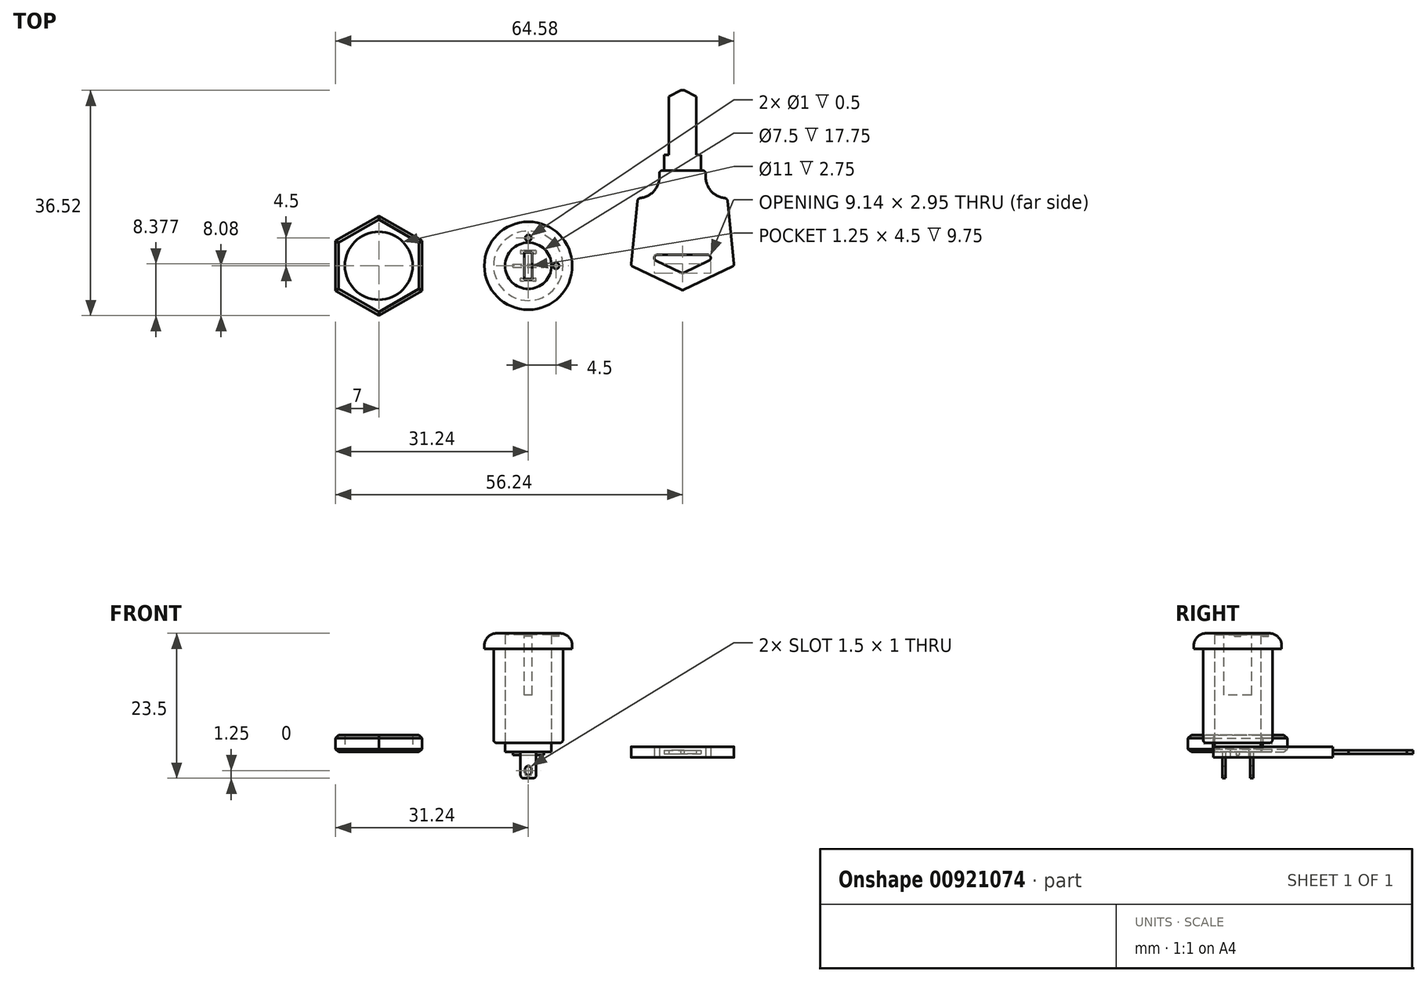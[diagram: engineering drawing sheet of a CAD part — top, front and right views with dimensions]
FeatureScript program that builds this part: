
annotation { "Feature Type Name" : "Feature", "Feature Type Description" : "" }
export const myFeature = defineFeature(function(context is Context, id is Id, definition is map)
    precondition{}
    {
        {
            var Q0;
            Q0=qCreatedBy(makeId("Top.planeOp"),FACE);
            var sketch = newSketch(context, id + "F0", { "sketchPlane" : qUnion([Q0])});
            skCircle(sketch, "E0", {"center": v(0, 0) * mm, "radius": 5.62 * mm});
            skCircle(sketch, "E1", {"center": v(0, 0) * mm, "radius": 7.12 * mm});
            skCircle(sketch, "E2", {"center": v(0, 0) * mm, "radius": 3.75 * mm});
            skSolve(sketch);
        }
        {
            var Q0;
            Q0=makeQuery(id+"F0.imprint","IMPRINT",FACE,{"disambiguationData":[TD([[makeQuery(id+"F0.imprint","IMPRINT",EDGE,{"derivedFrom":sQuery(id+"F0.wireOp",EDGE,"E2")}),1.0]])]});
            extrude(context, id + "F1", {"entities" : qUnion([Q0]), "depth" : 1.5 * mm, "offsetDistance" : 25 * mm});
        }
        {
            var Q0;
            Q0=makeQuery(id+"F0.imprint","IMPRINT",FACE,{"disambiguationData":[TD([[makeQuery(id+"F0.imprint","IMPRINT",EDGE,{"derivedFrom":sQuery(id+"F0.wireOp",EDGE,"E0")}),1.0]])]});
            var Q1;
            Q1=makeQuery(id+"F1.opExtrude","CAP_FACE",FACE,{"disambiguationData":[OSD([sQuery(id+"F0.wireOp",EDGE,"E2")])],"isStart":false});
            extrude(context, id + "F2", {"entities" : qUnion([Q0]), "depth" : 16.75 * mm, "offsetDistance" : 25 * mm, "hasSecondDirection" : true, "secondDirectionBound" : SecondDirectionBoundingType.UP_TO_SURFACE, "secondDirectionOppositeDirection" : false, "secondDirectionDepth" : 1.5 * mm, "secondDirectionBoundEntityFace" : qUnion([Q1])});
        }
        {
            var Q0;
            Q0=makeQuery(id+"F0.imprint","IMPRINT",FACE,{"disambiguationData":[TD([[makeQuery(id+"F0.imprint","IMPRINT",EDGE,{"derivedFrom":sQuery(id+"F0.wireOp",EDGE,"E0")}),-1.0]])]});
            var Q1;
            Q1=makeQuery(id+"F0.imprint","IMPRINT",FACE,{"disambiguationData":[TD([[makeQuery(id+"F0.imprint","IMPRINT",EDGE,{"derivedFrom":sQuery(id+"F0.wireOp",EDGE,"E0")}),1.0]])]});
            var Q2;
            Q2=makeQuery(id+"F2.opExtrude","CAP_FACE",FACE,{"disambiguationData":[OSD([sQuery(id+"F0.wireOp",EDGE,"E0"),sQuery(id+"F0.wireOp",EDGE,"E2")])],"isStart":false});
            var Q3;
            Q3=makeQuery(id+"F2.opExtrude","CAP_FACE",FACE,{"disambiguationData":[OSD([sQuery(id+"F0.wireOp",EDGE,"E0"),sQuery(id+"F0.wireOp",EDGE,"E2")])],"isStart":false});
            extrude(context, id + "F3", {"entities" : qUnion([Q0, Q1]), "operationType" : NewBodyOperationType.ADD, "endBound" : BoundingType.UP_TO_SURFACE, "depth" : (16.75 + 2.5) * mm, "endBoundEntityFace" : qUnion([Q2]), "hasOffset" : true, "offsetDistance" : 2.5 * mm, "offsetOppositeDirection" : true, "hasSecondDirection" : true, "secondDirectionBound" : SecondDirectionBoundingType.UP_TO_SURFACE, "secondDirectionOppositeDirection" : false, "secondDirectionDepth" : 16.75 * mm, "secondDirectionBoundEntityFace" : qUnion([Q3])});
        }
        {
            var Q0;
            Q0=makeQuery(id+"F1.opExtrude","CAP_FACE",FACE,{"disambiguationData":[OSD([sQuery(id+"F0.wireOp",EDGE,"E2")])],"isStart":false});
            var Q1;
            Q1=makeQuery(id+"F3.opExtrude","CAP_FACE",FACE,{"disambiguationData":[OSD([sQuery(id+"F0.wireOp",EDGE,"E1"),sQuery(id+"F0.wireOp",EDGE,"E2")])],"isStart":false});
            extrude(context, id + "F4", {"entities" : qUnion([Q0]), "endBound" : BoundingType.UP_TO_SURFACE, "depth" : 25 * mm, "endBoundEntityFace" : qUnion([Q1]), "hasOffset" : true, "offsetDistance" : .25 * mm});
        }
        {
            var Q0;
            Q0=makeQuery(id+"F3.opExtrude","CAP_FACE",FACE,{"disambiguationData":[OSD([sQuery(id+"F0.wireOp",EDGE,"E1")])],"isStart":false});
            var sketch = newSketch(context, id + "F5", { "sketchPlane" : qUnion([Q0])});
            skCircle(sketch, "E3", {"center": v(0, 4.5) * mm, "radius": 0.5 * mm});
            skCircle(sketch, "E4", {"center": v(4.5, 0) * mm, "radius": 0.5 * mm});
            skLineSegment(sketch, "E5", {"start": v(0, 4.5) * mm, "end": v(0, 0) * mm, "construction": true});
            skLineSegment(sketch, "E6", {"start": v(0, 0) * mm, "end": v(4.5, 0) * mm, "construction": true});
            skCircle(sketch, "E7.0", {"center": v(0, 0) * mm, "radius": 3.75 * mm});
            skLineSegment(sketch, "E8.bottom", {"start": v(0.63, 2.25) * mm, "end": v(-0.62, 2.25) * mm});
            skLineSegment(sketch, "E8.top", {"start": v(0.62, -2.25) * mm, "end": v(-0.63, -2.25) * mm});
            skLineSegment(sketch, "E8.left", {"start": v(0.63, 2.25) * mm, "end": v(0.62, -2.25) * mm});
            skLineSegment(sketch, "E8.right", {"start": v(-0.62, 2.25) * mm, "end": v(-0.63, -2.25) * mm});
            skSolve(sketch);
        }
        {
            var Q0;
            Q0=makeQuery(id+"F5.imprint","IMPRINT",FACE,{"disambiguationData":[TD([[makeQuery(id+"F5.imprint","IMPRINT",EDGE,{"derivedFrom":sQuery(id+"F5.wireOp",EDGE,"E8.bottom")}),1.0]])]});
            extrude(context, id + "F6", {"entities" : qUnion([Q0]), "operationType" : NewBodyOperationType.REMOVE, "oppositeDirection" : true, "depth" : 10 * mm, "offsetDistance" : 25 * mm});
        }
        {
            var Q0;
            Q0=makeQuery(id+"F5.imprint","IMPRINT",FACE,{"disambiguationData":[TD([[makeQuery(id+"F5.imprint","IMPRINT",EDGE,{"derivedFrom":sQuery(id+"F5.wireOp",EDGE,"E3")}),1.0]])]});
            var Q1;
            Q1=makeQuery(id+"F5.imprint","IMPRINT",FACE,{"disambiguationData":[TD([[makeQuery(id+"F5.imprint","IMPRINT",EDGE,{"derivedFrom":sQuery(id+"F5.wireOp",EDGE,"E4")}),1.0]])]});
            extrude(context, id + "F7", {"entities" : qUnion([Q0, Q1]), "operationType" : NewBodyOperationType.REMOVE, "oppositeDirection" : true, "depth" : .5 * mm, "offsetDistance" : 25 * mm});
        }
        {
            var Q0;
            Q0=makeQuery(id+"F5.imprint","IMPRINT",FACE,{"disambiguationData":[TD([[makeQuery(id+"F5.imprint","IMPRINT",EDGE,{"derivedFrom":sQuery(id+"F5.wireOp",EDGE,"E3")}),1.0]])]});
            var Q1;
            Q1=makeQuery(id+"F5.imprint","IMPRINT",FACE,{"disambiguationData":[TD([[makeQuery(id+"F5.imprint","IMPRINT",EDGE,{"derivedFrom":sQuery(id+"F5.wireOp",EDGE,"E4")}),1.0]])]});
            var Q2;
            Q2=makeQuery(id+"F7.boolean.opBoolean","COPY",FACE,{"derivedFrom":makeQuery(id+"F7.opExtrude","CAP_FACE",FACE,{"disambiguationData":[OSD([sQuery(id+"F5.wireOp",EDGE,"E3")])],"isStart":false})});
            var Q3;
            Q3=makeQuery(id+"F7.boolean.opBoolean","COPY",FACE,{"derivedFrom":makeQuery(id+"F7.opExtrude","CAP_FACE",FACE,{"disambiguationData":[OSD([sQuery(id+"F5.wireOp",EDGE,"E3")])],"isStart":false})});
            extrude(context, id + "F8", {"entities" : qUnion([Q0, Q1]), "endBound" : BoundingType.UP_TO_SURFACE, "oppositeDirection" : true, "depth" : 25 * mm, "endBoundEntityFace" : qUnion([Q2]), "offsetDistance" : .25 * mm, "hasSecondDirection" : true, "secondDirectionBound" : SecondDirectionBoundingType.UP_TO_SURFACE, "secondDirectionOppositeDirection" : true, "secondDirectionDepth" : 25 * mm, "secondDirectionBoundEntityFace" : qUnion([Q3]), "hasSecondDirectionOffset" : true, "secondDirectionOffsetDistance" : .25 * mm});
        }
        {
            var Q0;
            Q0=qCreatedBy(makeId("Front.planeOp"),FACE);
            var sketch = newSketch(context, id + "F9", { "sketchPlane" : qUnion([Q0])});
            skLineSegment(sketch, "E9.bottom", {"start": v(1.25, 0) * mm, "end": v(-1.25, 0) * mm});
            skLineSegment(sketch, "E9.top", {"start": v(1.25, -4.25) * mm, "end": v(-1.25, -4.25) * mm});
            skLineSegment(sketch, "E9.left", {"start": v(1.25, 0) * mm, "end": v(1.25, -4.25) * mm});
            skLineSegment(sketch, "E9.right", {"start": v(-1.25, 0) * mm, "end": v(-1.25, -4.25) * mm});
            skPoint(sketch, "E10", {"position": v(0, 0) * mm});
            skLineSegment(sketch, "E11.bottom", {"start": v(-0.5, -2.25) * mm, "end": v(0.5, -2.25) * mm});
            skLineSegment(sketch, "E11.top", {"start": v(-0.5, -3.75) * mm, "end": v(0.5, -3.75) * mm});
            skLineSegment(sketch, "E11.left", {"start": v(-0.5, -2.25) * mm, "end": v(-0.5, -3.75) * mm});
            skLineSegment(sketch, "E11.right", {"start": v(0.5, -2.25) * mm, "end": v(0.5, -3.75) * mm});
            skPoint(sketch, "E11.middle", {"position": v(0, -3) * mm});
            skLineSegment(sketch, "E12.bottom", {"start": v(-2.5, 0) * mm, "end": v(2.5, 0) * mm});
            skLineSegment(sketch, "E12.top", {"start": v(-2.5, -0.5) * mm, "end": v(2.5, -0.5) * mm});
            skLineSegment(sketch, "E12.left", {"start": v(-2.5, 0) * mm, "end": v(-2.5, -0.5) * mm});
            skLineSegment(sketch, "E12.right", {"start": v(2.5, 0) * mm, "end": v(2.5, -0.5) * mm});
            skSolve(sketch);
        }
        {
            var Q0;
            {var subQ5=sQuery(id+"F9.wireOp",EDGE,"E12.left");Q0=makeQuery(id+"F9.imprint","IMPRINT",FACE,{"disambiguationData":[TD([[makeQuery(id+"F9.imprint","IMPRINT",EDGE,{"derivedFrom":subQ5}),1.0]])]});}
            var Q1;
            {var subQ0=sQuery(id+"F9.wireOp",EDGE,"E12.bottom");var subQ1=sQuery(id+"F9.wireOp",EDGE,"E9.left");var subQ2=makeQuery(id+"F9.imprint","INTERSECT",VERTEX,{"derivedFrom":[subQ1,subQ0]});Q1=makeQuery(id+"F9.imprint","IMPRINT",FACE,{"disambiguationData":[TD([[makeQuery(id+"F9.imprint","IMPRINT",EDGE,{"disambiguationData":[TD([[subQ2,-1.0]])],"derivedFrom":subQ1}),-1.0]])]});}
            var Q2;
            {var subQ5=sQuery(id+"F9.wireOp",EDGE,"E12.right");Q2=makeQuery(id+"F9.imprint","IMPRINT",FACE,{"disambiguationData":[TD([[makeQuery(id+"F9.imprint","IMPRINT",EDGE,{"derivedFrom":subQ5}),-1.0]])]});}
            extrude(context, id + "F10", {"entities" : qUnion([Q0, Q1, Q2]), "operationType" : NewBodyOperationType.ADD, "endBound" : BoundingType.SYMMETRIC, "depth" : .5 * mm, "offsetDistance" : 25 * mm});
        }
        {
            var Q0;
            {var subQ1=sQuery(id+"F9.wireOp",EDGE,"E9.top");Q0=makeQuery(id+"F9.imprint","IMPRINT",FACE,{"disambiguationData":[TD([[makeQuery(id+"F9.imprint","IMPRINT",EDGE,{"derivedFrom":subQ1}),-1.0]])]});}
            var Q1;
            {var subQ0=sQuery(id+"F9.wireOp",EDGE,"E12.bottom");var subQ1=sQuery(id+"F9.wireOp",EDGE,"E9.left");var subQ2=makeQuery(id+"F9.imprint","INTERSECT",VERTEX,{"derivedFrom":[subQ1,subQ0]});Q1=makeQuery(id+"F9.imprint","IMPRINT",FACE,{"disambiguationData":[TD([[makeQuery(id+"F9.imprint","IMPRINT",EDGE,{"disambiguationData":[TD([[subQ2,-1.0]])],"derivedFrom":subQ1}),-1.0]])]});}
            extrude(context, id + "F11", {"entities" : qUnion([Q0, Q1]), "depth" : 2.5 * mm, "offsetDistance" : 25 * mm, "hasSecondDirection" : true, "secondDirectionOppositeDirection" : false, "secondDirectionDepth" : 2 * mm});
        }
        {
            var Q0;
            {var subQ1=sQuery(id+"F9.wireOp",EDGE,"E9.top");Q0=makeQuery(id+"F9.imprint","IMPRINT",FACE,{"disambiguationData":[TD([[makeQuery(id+"F9.imprint","IMPRINT",EDGE,{"derivedFrom":subQ1}),-1.0]])]});}
            var Q1;
            {var subQ0=sQuery(id+"F9.wireOp",EDGE,"E12.bottom");var subQ1=sQuery(id+"F9.wireOp",EDGE,"E9.left");var subQ2=makeQuery(id+"F9.imprint","INTERSECT",VERTEX,{"derivedFrom":[subQ1,subQ0]});Q1=makeQuery(id+"F9.imprint","IMPRINT",FACE,{"disambiguationData":[TD([[makeQuery(id+"F9.imprint","IMPRINT",EDGE,{"disambiguationData":[TD([[subQ2,-1.0]])],"derivedFrom":subQ1}),-1.0]])]});}
            extrude(context, id + "F12", {"entities" : qUnion([Q0, Q1]), "oppositeDirection" : true, "depth" : 2.5 * mm, "offsetDistance" : 25 * mm, "hasSecondDirection" : true, "secondDirectionOppositeDirection" : true, "secondDirectionDepth" : 2 * mm});
        }
        {
            var Q0;
            Q0=makeQuery(id+"F3.opExtrude","CAP_EDGE",EDGE,{"disambiguationData":[OSD([sQuery(id+"F0.wireOp",EDGE,"E1")])],"isStart":false});
            fillet(context, id + "F13", {"entities" : qUnion([Q0]), "radius" : 2 * mm, "tangentPropagation" : true, "allowEdgeOverflow" : false});
        }
        {
            var Q0;
            Q0=makeQuery(id+"F12.opExtrude","SWEPT_EDGE",EDGE,{"disambiguationData":[OSD([sQuery(id+"F9.wireOp",EDGE,"E9.top"),sQuery(id+"F9.wireOp",EDGE,"E9.left")])]});
            var Q1;
            Q1=makeQuery(id+"F12.opExtrude","SWEPT_EDGE",EDGE,{"disambiguationData":[OSD([sQuery(id+"F9.wireOp",EDGE,"E9.top"),sQuery(id+"F9.wireOp",EDGE,"E9.right")])]});
            var Q2;
            Q2=makeQuery(id+"F11.opExtrude","SWEPT_EDGE",EDGE,{"disambiguationData":[OSD([sQuery(id+"F9.wireOp",EDGE,"E9.top"),sQuery(id+"F9.wireOp",EDGE,"E9.left")])]});
            var Q3;
            Q3=makeQuery(id+"F11.opExtrude","SWEPT_EDGE",EDGE,{"disambiguationData":[OSD([sQuery(id+"F9.wireOp",EDGE,"E9.top"),sQuery(id+"F9.wireOp",EDGE,"E9.right")])]});
            var Q4;
            Q4=makeQuery(id+"F2.opExtrude","CAP_EDGE",EDGE,{"disambiguationData":[OSD([sQuery(id+"F0.wireOp",EDGE,"E0")])],"isStart":true});
            var Q5;
            Q5=makeQuery(id+"F12.opExtrude","SWEPT_EDGE",EDGE,{"disambiguationData":[OSD([sQuery(id+"F9.wireOp",EDGE,"E11.bottom"),sQuery(id+"F9.wireOp",EDGE,"E11.left")])]});
            var Q6;
            Q6=makeQuery(id+"F12.opExtrude","SWEPT_EDGE",EDGE,{"disambiguationData":[OSD([sQuery(id+"F9.wireOp",EDGE,"E11.bottom"),sQuery(id+"F9.wireOp",EDGE,"E11.right")])]});
            var Q7;
            Q7=makeQuery(id+"F12.opExtrude","SWEPT_EDGE",EDGE,{"disambiguationData":[OSD([sQuery(id+"F9.wireOp",EDGE,"E11.top"),sQuery(id+"F9.wireOp",EDGE,"E11.right")])]});
            var Q8;
            Q8=makeQuery(id+"F12.opExtrude","SWEPT_EDGE",EDGE,{"disambiguationData":[OSD([sQuery(id+"F9.wireOp",EDGE,"E11.top"),sQuery(id+"F9.wireOp",EDGE,"E11.left")])]});
            var Q9;
            Q9=makeQuery(id+"F11.opExtrude","SWEPT_EDGE",EDGE,{"disambiguationData":[OSD([sQuery(id+"F9.wireOp",EDGE,"E11.bottom"),sQuery(id+"F9.wireOp",EDGE,"E11.left")])]});
            var Q10;
            Q10=makeQuery(id+"F11.opExtrude","SWEPT_EDGE",EDGE,{"disambiguationData":[OSD([sQuery(id+"F9.wireOp",EDGE,"E11.bottom"),sQuery(id+"F9.wireOp",EDGE,"E11.right")])]});
            var Q11;
            Q11=makeQuery(id+"F11.opExtrude","SWEPT_EDGE",EDGE,{"disambiguationData":[OSD([sQuery(id+"F9.wireOp",EDGE,"E11.top"),sQuery(id+"F9.wireOp",EDGE,"E11.right")])]});
            var Q12;
            Q12=makeQuery(id+"F11.opExtrude","SWEPT_EDGE",EDGE,{"disambiguationData":[OSD([sQuery(id+"F9.wireOp",EDGE,"E11.top"),sQuery(id+"F9.wireOp",EDGE,"E11.left")])]});
            fillet(context, id + "F14", {"entities" : qUnion([Q0, Q1, Q2, Q3, Q4, Q5, Q6, Q7, Q8, Q9, Q10, Q11, Q12]), "radius" : .5 * mm, "tangentPropagation" : true, "allowEdgeOverflow" : false});
        }
        {
            var Q0;
            Q0=qCreatedBy(makeId("Top.planeOp"),FACE);
            var sketch = newSketch(context, id + "F15", { "sketchPlane" : qUnion([Q0])});
            skCircle(sketch, "E13", {"center": v(-24.24, 0) * mm, "radius": 5.5 * mm});
            skCircle(sketch, "E14.cCircle", {"center": v(-24.24, 0) * mm, "radius": 7 * mm, "construction": true});
            skLineSegment(sketch, "E14.0", {"start": v(-31.24, -4.04) * mm, "end": v(-31.24, 4.04) * mm});
            skLineSegment(sketch, "E14.1", {"start": v(-31.24, 4.04) * mm, "end": v(-24.24, 8.08) * mm});
            skLineSegment(sketch, "E14.2", {"start": v(-24.24, 8.08) * mm, "end": v(-17.24, 4.04) * mm});
            skLineSegment(sketch, "E14.3", {"start": v(-17.24, 4.04) * mm, "end": v(-17.24, -4.04) * mm});
            skLineSegment(sketch, "E14.4", {"start": v(-17.24, -4.04) * mm, "end": v(-24.24, -8.08) * mm});
            skLineSegment(sketch, "E14.5", {"start": v(-24.24, -8.08) * mm, "end": v(-31.24, -4.04) * mm});
            skPoint(sketch, "E14.0.midPoint", {"position": v(-31.24, 0) * mm});
            skSolve(sketch);
        }
        {
            var Q0;
            Q0=makeQuery(id+"F15.imprint","IMPRINT",FACE,{"disambiguationData":[TD([[makeQuery(id+"F15.imprint","IMPRINT",EDGE,{"derivedFrom":sQuery(id+"F15.wireOp",EDGE,"E13")}),-1.0]])]});
            extrude(context, id + "F16", {"entities" : qUnion([Q0]), "depth" : 2.75 * mm, "offsetDistance" : 25 * mm});
        }
        {
            var Q0;
            Q0=makeQuery(id+"F16.opExtrude","CAP_EDGE",EDGE,{"disambiguationData":[OSD([sQuery(id+"F15.wireOp",EDGE,"E14.4")])],"isStart":false});
            var Q1;
            Q1=makeQuery(id+"F16.opExtrude","CAP_EDGE",EDGE,{"disambiguationData":[OSD([sQuery(id+"F15.wireOp",EDGE,"E14.5")])],"isStart":false});
            var Q2;
            Q2=makeQuery(id+"F16.opExtrude","CAP_EDGE",EDGE,{"disambiguationData":[OSD([sQuery(id+"F15.wireOp",EDGE,"E14.0")])],"isStart":false});
            var Q3;
            Q3=makeQuery(id+"F16.opExtrude","CAP_EDGE",EDGE,{"disambiguationData":[OSD([sQuery(id+"F15.wireOp",EDGE,"E14.1")])],"isStart":false});
            var Q4;
            Q4=makeQuery(id+"F16.opExtrude","CAP_EDGE",EDGE,{"disambiguationData":[OSD([sQuery(id+"F15.wireOp",EDGE,"E14.2")])],"isStart":false});
            var Q5;
            Q5=makeQuery(id+"F16.opExtrude","CAP_EDGE",EDGE,{"disambiguationData":[OSD([sQuery(id+"F15.wireOp",EDGE,"E14.3")])],"isStart":false});
            var Q6;
            Q6=makeQuery(id+"F16.opExtrude","CAP_EDGE",EDGE,{"disambiguationData":[OSD([sQuery(id+"F15.wireOp",EDGE,"E14.2")])],"isStart":true});
            var Q7;
            Q7=makeQuery(id+"F16.opExtrude","CAP_EDGE",EDGE,{"disambiguationData":[OSD([sQuery(id+"F15.wireOp",EDGE,"E14.1")])],"isStart":true});
            var Q8;
            Q8=makeQuery(id+"F16.opExtrude","CAP_EDGE",EDGE,{"disambiguationData":[OSD([sQuery(id+"F15.wireOp",EDGE,"E14.0")])],"isStart":true});
            var Q9;
            Q9=makeQuery(id+"F16.opExtrude","CAP_EDGE",EDGE,{"disambiguationData":[OSD([sQuery(id+"F15.wireOp",EDGE,"E14.5")])],"isStart":true});
            var Q10;
            Q10=makeQuery(id+"F16.opExtrude","CAP_EDGE",EDGE,{"disambiguationData":[OSD([sQuery(id+"F15.wireOp",EDGE,"E14.4")])],"isStart":true});
            var Q11;
            Q11=makeQuery(id+"F16.opExtrude","CAP_EDGE",EDGE,{"disambiguationData":[OSD([sQuery(id+"F15.wireOp",EDGE,"E14.3")])],"isStart":true});
            chamfer(context, id + "F17", {"entities" : qUnion([Q0, Q1, Q2, Q3, Q4, Q5, Q6, Q7, Q8, Q9, Q10, Q11]), "width" : .5 * mm, "tangentPropagation" : true});
        }
        {
            var Q0;
            Q0=qCreatedBy(makeId("Top.planeOp"),FACE);
            var sketch = newSketch(context, id + "F18", { "sketchPlane" : qUnion([Q0])});
            skLineSegment(sketch, "E15", {"start": v(16.63, 0) * mm, "end": v(25, -4) * mm});
            skLineSegment(sketch, "E16", {"start": v(25, -4) * mm, "end": v(33.38, 0) * mm});
            skLineSegment(sketch, "E17", {"start": v(33.38, 0) * mm, "end": v(32.25, 10.94) * mm});
            skLineSegment(sketch, "E18", {"start": v(16.63, 0) * mm, "end": v(17.75, 10.94) * mm});
            skArc(sketch, "E19", {"start": v(17.75, 10.94) * mm, "mid": v(20.56, 12.35) * mm, "end": v(21.13, 15.44) * mm});
            skArc(sketch, "E20", {"start": v(28.88, 15.44) * mm, "mid": v(29.44, 12.35) * mm, "end": v(32.25, 10.94) * mm});
            skLineSegment(sketch, "E21", {"start": v(21.13, 15.44) * mm, "end": v(28.88, 15.44) * mm});
            skLineSegment(sketch, "E22.0", {"start": v(25, -1.23) * mm, "end": v(31.28, 1.77) * mm});
            skLineSegment(sketch, "E22.1", {"start": v(18.72, 1.77) * mm, "end": v(25, -1.23) * mm});
            skLineSegment(sketch, "E23", {"start": v(18.72, 1.77) * mm, "end": v(31.28, 1.77) * mm});
            skLineSegment(sketch, "E24.bottom", {"start": v(27.25, 15.44) * mm, "end": v(22.75, 15.44) * mm});
            skLineSegment(sketch, "E24.top", {"start": v(27.25, 28.44) * mm, "end": v(22.75, 28.44) * mm});
            skLineSegment(sketch, "E24.left", {"start": v(27.25, 15.44) * mm, "end": v(27.25, 28.44) * mm});
            skLineSegment(sketch, "E24.right", {"start": v(22.75, 15.44) * mm, "end": v(22.75, 28.44) * mm});
            skPoint(sketch, "E25", {"position": v(25, 15.44) * mm});
            skLineSegment(sketch, "E26.bottom", {"start": v(22, 15.44) * mm, "end": v(28, 15.44) * mm});
            skLineSegment(sketch, "E26.top", {"start": v(22, 17.94) * mm, "end": v(28, 17.94) * mm});
            skLineSegment(sketch, "E26.left", {"start": v(22, 15.44) * mm, "end": v(22, 17.94) * mm});
            skLineSegment(sketch, "E26.right", {"start": v(28, 15.44) * mm, "end": v(28, 17.94) * mm});
            skSolve(sketch);
        }
        {
            var Q0;
            Q0=makeQuery(id+"F18.imprint","IMPRINT",FACE,{"disambiguationData":[TD([[makeQuery(id+"F18.imprint","IMPRINT",EDGE,{"derivedFrom":sQuery(id+"F18.wireOp",EDGE,"E15")}),1.0]])]});
            extrude(context, id + "F19", {"entities" : qUnion([Q0]), "endBound" : BoundingType.SYMMETRIC, "depth" : (3.5 / 2) * mm, "offsetDistance" : 25 * mm});
        }
        {
            var Q0;
            {var subQ0=sQuery(id+"F18.wireOp",EDGE,"E26.bottom");var subQ1=sQuery(id+"F18.wireOp",EDGE,"E24.left");var subQ2=makeQuery(id+"F18.imprint","INTERSECT",VERTEX,{"derivedFrom":[subQ1,subQ0]});Q0=makeQuery(id+"F18.imprint","IMPRINT",FACE,{"disambiguationData":[TD([[makeQuery(id+"F18.imprint","IMPRINT",EDGE,{"disambiguationData":[TD([[subQ2,-1.0]])],"derivedFrom":subQ1}),1.0]])]});}
            var Q1;
            {var subQ5=sQuery(id+"F18.wireOp",EDGE,"E26.right");Q1=makeQuery(id+"F18.imprint","IMPRINT",FACE,{"disambiguationData":[TD([[makeQuery(id+"F18.imprint","IMPRINT",EDGE,{"derivedFrom":subQ5}),1.0]])]});}
            var Q2;
            {var subQ5=sQuery(id+"F18.wireOp",EDGE,"E26.left");Q2=makeQuery(id+"F18.imprint","IMPRINT",FACE,{"disambiguationData":[TD([[makeQuery(id+"F18.imprint","IMPRINT",EDGE,{"derivedFrom":subQ5}),-1.0]])]});}
            var Q3;
            {var subQ0=sQuery(id+"F18.wireOp",EDGE,"E24.top");Q3=makeQuery(id+"F18.imprint","IMPRINT",FACE,{"disambiguationData":[TD([[makeQuery(id+"F18.imprint","IMPRINT",EDGE,{"derivedFrom":subQ0}),1.0]])]});}
            extrude(context, id + "F20", {"entities" : qUnion([Q0, Q1, Q2, Q3]), "endBound" : BoundingType.SYMMETRIC, "depth" : (1.25 / 2) * mm, "offsetDistance" : 25 * mm});
        }
        {
            var Q0;
            Q0=makeQuery(id+"F19.opExtrude","SWEPT_EDGE",EDGE,{"disambiguationData":[OSD([sQuery(id+"F18.wireOp",EDGE,"E22.1"),sQuery(id+"F18.wireOp",EDGE,"E23")])]});
            var Q1;
            Q1=makeQuery(id+"F19.opExtrude","SWEPT_EDGE",EDGE,{"disambiguationData":[OSD([sQuery(id+"F18.wireOp",EDGE,"E22.0"),sQuery(id+"F18.wireOp",EDGE,"E22.1")])]});
            var Q2;
            Q2=makeQuery(id+"F19.opExtrude","SWEPT_EDGE",EDGE,{"disambiguationData":[OSD([sQuery(id+"F18.wireOp",EDGE,"E22.0"),sQuery(id+"F18.wireOp",EDGE,"E23")])]});
            var Q3;
            Q3=makeQuery(id+"F19.opExtrude","SWEPT_EDGE",EDGE,{"disambiguationData":[OSD([sQuery(id+"F18.wireOp",EDGE,"E16"),sQuery(id+"F18.wireOp",EDGE,"E17")])]});
            var Q4;
            Q4=makeQuery(id+"F19.opExtrude","SWEPT_EDGE",EDGE,{"disambiguationData":[OSD([sQuery(id+"F18.wireOp",EDGE,"E15"),sQuery(id+"F18.wireOp",EDGE,"E16")])]});
            var Q5;
            Q5=makeQuery(id+"F19.opExtrude","SWEPT_EDGE",EDGE,{"disambiguationData":[OSD([sQuery(id+"F18.wireOp",EDGE,"E15"),sQuery(id+"F18.wireOp",EDGE,"E18")])]});
            var Q6;
            Q6=makeQuery(id+"F19.opExtrude","SWEPT_EDGE",EDGE,{"disambiguationData":[OSD([sQuery(id+"F18.wireOp",EDGE,"E17"),sQuery(id+"F18.wireOp",EDGE,"E20")])]});
            var Q7;
            Q7=makeQuery(id+"F19.opExtrude","SWEPT_EDGE",EDGE,{"disambiguationData":[OSD([sQuery(id+"F18.wireOp",EDGE,"E20"),sQuery(id+"F18.wireOp",EDGE,"E21")])]});
            var Q8;
            Q8=makeQuery(id+"F19.opExtrude","SWEPT_EDGE",EDGE,{"disambiguationData":[OSD([sQuery(id+"F18.wireOp",EDGE,"E19"),sQuery(id+"F18.wireOp",EDGE,"E21")])]});
            var Q9;
            Q9=makeQuery(id+"F19.opExtrude","SWEPT_EDGE",EDGE,{"disambiguationData":[OSD([sQuery(id+"F18.wireOp",EDGE,"E18"),sQuery(id+"F18.wireOp",EDGE,"E19")])]});
            fillet(context, id + "F21", {"entities" : qUnion([Q0, Q1, Q2, Q3, Q4, Q5, Q6, Q7, Q8, Q9]), "radius" : .5 * mm, "tangentPropagation" : true, "allowEdgeOverflow" : false});
        }
        {
            var Q0;
            Q0=makeQuery(id+"F20.opExtrude","SWEPT_EDGE",EDGE,{"disambiguationData":[OSD([sQuery(id+"F18.wireOp",EDGE,"E24.top"),sQuery(id+"F18.wireOp",EDGE,"E24.left")])]});
            var Q1;
            Q1=makeQuery(id+"F20.opExtrude","SWEPT_EDGE",EDGE,{"disambiguationData":[OSD([sQuery(id+"F18.wireOp",EDGE,"E24.top"),sQuery(id+"F18.wireOp",EDGE,"E24.right")])]});
            chamfer(context, id + "F22", {"entities" : qUnion([Q0, Q1]), "chamferType" : ChamferType.TWO_OFFSETS, "width1" : 2 * mm, "oppositeDirection" : false, "width2" : 1 * mm, "tangentPropagation" : true});
        }
    });
